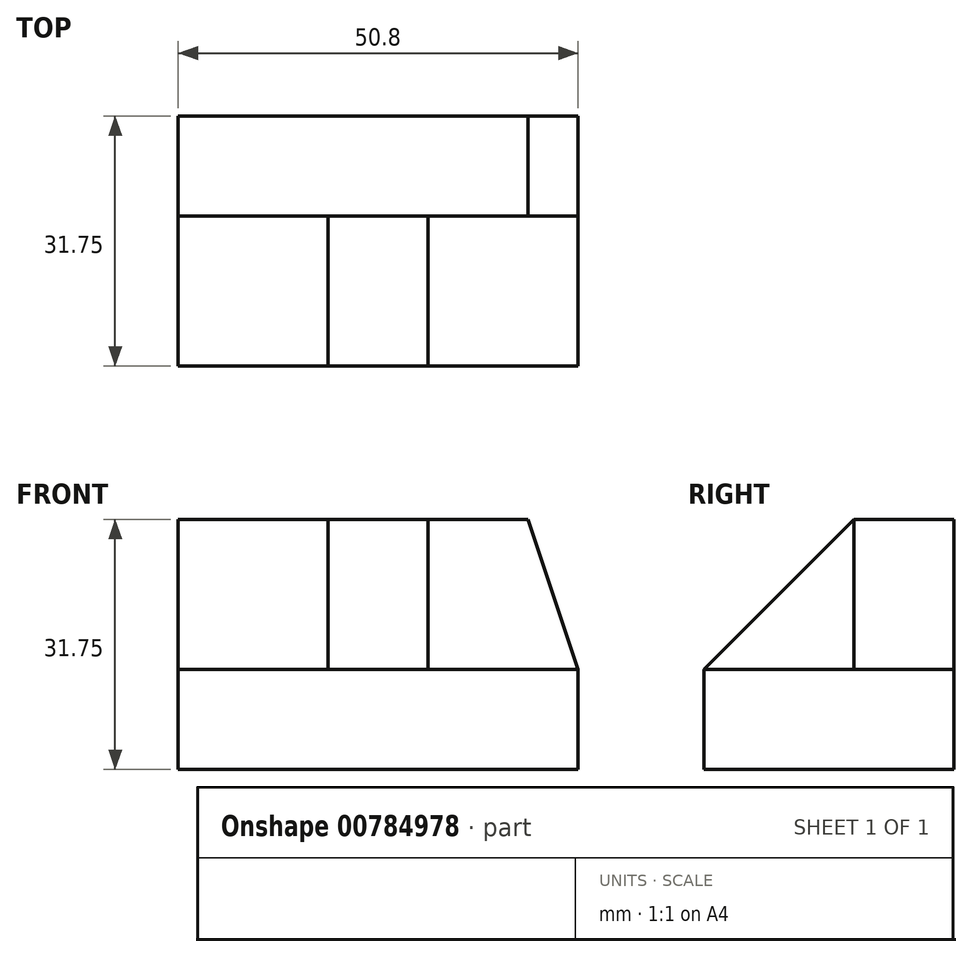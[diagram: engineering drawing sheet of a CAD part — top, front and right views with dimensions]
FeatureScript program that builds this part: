
annotation { "Feature Type Name" : "Feature", "Feature Type Description" : "" }
export const myFeature = defineFeature(function(context is Context, id is Id, definition is map)
    precondition{}
    {
        {
            var Q0;
            Q0=qCreatedBy(makeId("Right.planeOp"),FACE);
            var sketch = newSketch(context, id + "F0", { "sketchPlane" : qUnion([Q0])});
            skLineSegment(sketch, "E0", {"start": v(0, 0) * mm, "end": v(-19.05, 0) * mm});
            skLineSegment(sketch, "E1", {"start": v(-19.05, 0) * mm, "end": v(-19.05, -12.7) * mm});
            skLineSegment(sketch, "E2", {"start": v(-19.05, -12.7) * mm, "end": v(12.7, -12.7) * mm});
            skLineSegment(sketch, "E3", {"start": v(12.7, -12.7) * mm, "end": v(12.7, 19.05) * mm});
            skLineSegment(sketch, "E4", {"start": v(0, 19.05) * mm, "end": v(0, 0) * mm});
            skLineSegment(sketch, "E5", {"start": v(0, 19.05) * mm, "end": v(12.7, 19.05) * mm});
            skSolve(sketch);
        }
        {
            var Q0;
            Q0 = qSketchRegion(id + "F0", true);
            extrude(context, id + "F1", {"entities" : qUnion([Q0]), "depth" : 50.8 * mm, "offsetDistance" : 25.4 * mm});
        }
        {
            var Q0;
            Q0=makeQuery(id+"F1.opExtrude","SWEPT_FACE",FACE,{"disambiguationData":[OSD([sQuery(id+"F0.wireOp",EDGE,"E4")])]});
            var sketch = newSketch(context, id + "F2", { "sketchPlane" : qUnion([Q0])});
            skLineSegment(sketch, "E6", {"start": v(50.8, 19.05) * mm, "end": v(44.45, 19.05) * mm});
            skLineSegment(sketch, "E7", {"start": v(44.45, 19.05) * mm, "end": v(50.8, 0) * mm});
            skSolve(sketch);
        }
        {
            var Q0;
            Q0 = qSketchRegion(id + "F2", true);
            var Q1;
            Q1=makeQuery(id+"F2.imprint","IMPRINT",FACE,{"disambiguationData":[TD([[makeQuery(id+"F2.imprint","IMPRINT",EDGE,{"derivedFrom":sQuery(id+"F2.wireOp",EDGE,"E6")}),1.0]])]});
            extrude(context, id + "F3", {"entities" : qUnion([Q0, Q1]), "operationType" : NewBodyOperationType.REMOVE, "oppositeDirection" : true, "depth" : 25.4 * mm, "offsetDistance" : 25.4 * mm});
        }
        {
            var Q0;
            Q0=makeQuery(id+"F1.opExtrude","SWEPT_FACE",FACE,{"disambiguationData":[OSD([sQuery(id+"F0.wireOp",EDGE,"E4")])]});
            var sketch = newSketch(context, id + "F4", { "sketchPlane" : qUnion([Q0])});
            skLineSegment(sketch, "E8", {"start": v(0, 0) * mm, "end": v(19.05, 0) * mm});
            skLineSegment(sketch, "E9", {"start": v(50.8, 0) * mm, "end": v(31.75, 0) * mm});
            skLineSegment(sketch, "E10", {"start": v(31.75, 0) * mm, "end": v(31.75, 19.05) * mm});
            skLineSegment(sketch, "E11", {"start": v(19.05, 0) * mm, "end": v(19.05, 19.05) * mm});
            skLineSegment(sketch, "E12", {"start": v(19.05, 19.05) * mm, "end": v(31.75, 19.05) * mm});
            skSolve(sketch);
        }
        {
            var Q0;
            Q0 = qSketchRegion(id + "F4", true);
            var Q1;
            {var subQ0=sQuery(id+"F4.wireOp",EDGE,"E10");Q1=makeQuery(id+"F4.imprint","IMPRINT",FACE,{"disambiguationData":[TD([[makeQuery(id+"F4.imprint","IMPRINT",EDGE,{"derivedFrom":subQ0}),1.0]])]});}
            extrude(context, id + "F5", {"entities" : qUnion([Q0, Q1]), "operationType" : NewBodyOperationType.ADD, "depth" : 19.05 * mm, "offsetDistance" : 25.4 * mm});
        }
        {
            var Q0;
            Q0=makeQuery(id+"F5.opExtrude","SWEPT_FACE",FACE,{"disambiguationData":[OSD([sQuery(id+"F4.wireOp",EDGE,"E10")])]});
            var sketch = newSketch(context, id + "F6", { "sketchPlane" : qUnion([Q0])});
            skLineSegment(sketch, "E13", {"start": v(-19.05, 0) * mm, "end": v(0, 19.05) * mm});
            skSolve(sketch);
        }
        {
            var Q0;
            Q0 = qSketchRegion(id + "F6", true);
            var Q1;
            Q1=makeQuery(id+"F6.imprint","IMPRINT",FACE,{"disambiguationData":[TD([[makeQuery(id+"F6.imprint","IMPRINT",EDGE,{"derivedFrom":sQuery(id+"F6.wireOp",EDGE,"E13")}),1.0]])]});
            extrude(context, id + "F7", {"entities" : qUnion([Q0, Q1]), "operationType" : NewBodyOperationType.REMOVE, "oppositeDirection" : true, "depth" : 25.4 * mm, "offsetDistance" : 25.4 * mm});
        }
    });
